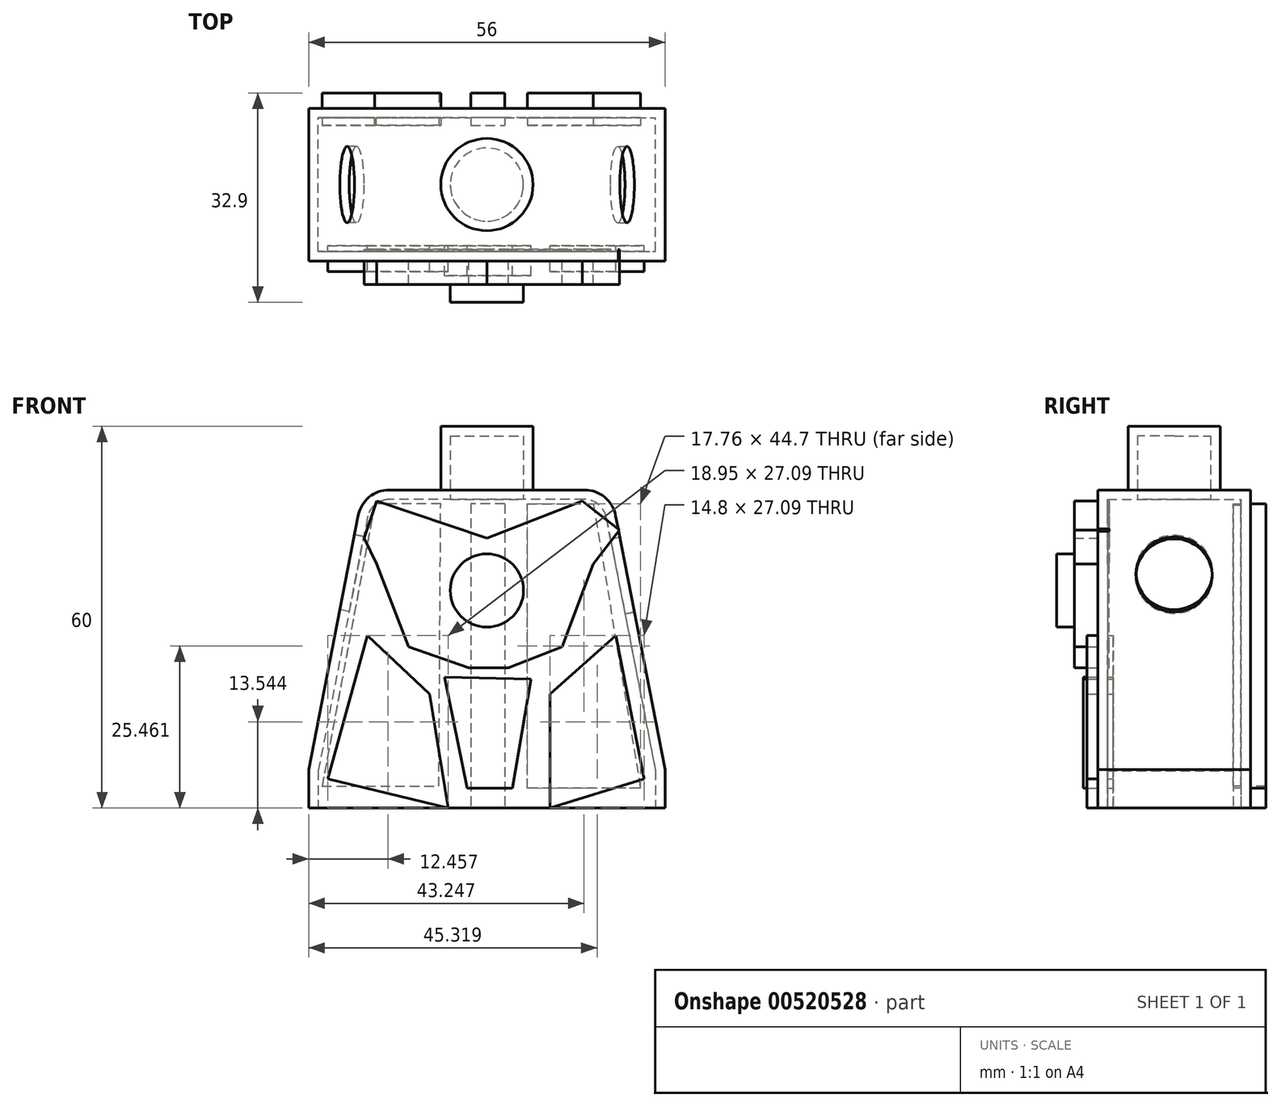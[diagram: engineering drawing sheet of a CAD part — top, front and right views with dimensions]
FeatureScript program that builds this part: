
annotation { "Feature Type Name" : "Feature", "Feature Type Description" : "" }
export const myFeature = defineFeature(function(context is Context, id is Id, definition is map)
    precondition{}
    {
        {
            var Q0;
            Q0=qCreatedBy(makeId("Front.planeOp"),FACE);
            var sketch = newSketch(context, id + "F0", { "sketchPlane" : qUnion([Q0])});
            skLineSegment(sketch, "E0", {"start": v(0, 0) * mm, "end": v(0, 50) * mm});
            skLineSegment(sketch, "E1", {"start": v(0, 50) * mm, "end": v(-6.67, 50) * mm});
            skLineSegment(sketch, "E2", {"start": v(-6.67, 50) * mm, "end": v(-6.67, 50) * mm});
            skLineSegment(sketch, "E3", {"start": v(-6.67, 50) * mm, "end": v(-15.33, 50) * mm});
            skLineSegment(sketch, "E4", {"start": v(-20.23, 45.95) * mm, "end": v(-28, 6) * mm});
            skLineSegment(sketch, "E5", {"start": v(-28, 6) * mm, "end": v(-28, 0) * mm});
            skLineSegment(sketch, "E6", {"start": v(-28, 0) * mm, "end": v(0, 0) * mm});
            skPoint(sketch, "E7.visualSharp", {"position": v(-19.45, 50) * mm});
            skArc(sketch, "E7.filletArc", {"start": v(-15.33, 50) * mm, "mid": v(-18.5, 48.86) * mm, "end": v(-20.23, 45.95) * mm});
            skLineSegment(sketch, "E8", {"start": v(-28, 6) * mm, "end": v(-28, 38.6) * mm, "construction": true});
            skSolve(sketch);
        }
        {
            var Q0;
            Q0=makeQuery(id+"F0.imprint","IMPRINT",FACE,{"disambiguationData":[TD([[makeQuery(id+"F0.imprint","IMPRINT",EDGE,{"derivedFrom":sQuery(id+"F0.wireOp",EDGE,"E0")}),1.0]])]});
            extrude(context, id + "F1", {"entities" : qUnion([Q0]), "endBound" : BoundingType.SYMMETRIC, "depth" : 24 * mm});
        }
        {
            var Q0;
            Q0=makeQuery(id+"F1.opExtrude","SWEPT_BODY",BODY,{"disambiguationData":[OSD([sQuery(id+"F0.wireOp",EDGE,"E0"),sQuery(id+"F0.wireOp",EDGE,"E1"),sQuery(id+"F0.wireOp",EDGE,"E2"),sQuery(id+"F0.wireOp",EDGE,"E3"),sQuery(id+"F0.wireOp",EDGE,"E4"),sQuery(id+"F0.wireOp",EDGE,"E5"),sQuery(id+"F0.wireOp",EDGE,"E6"),sQuery(id+"F0.wireOp",EDGE,"E7.filletArc")])]});
            var Q1;
            Q1=qCreatedBy(makeId("Right.planeOp"),FACE);
            mirror(context, id + "F2", {"operationType" : NewBodyOperationType.ADD, "entities" : qUnion([Q0]), "mirrorPlane" : qUnion([Q1])});
        }
        {
            var Q0;
            {var subQ0=makeQuery(id+"F1.opExtrude","SWEPT_FACE",FACE,{"disambiguationData":[OSD([sQuery(id+"F0.wireOp",EDGE,"E1"),sQuery(id+"F0.wireOp",EDGE,"E3")])]});Q0=makeQuery(id+"F2.boolean.opBoolean","MERGE",FACE,{"derivedFrom":[subQ0,makeQuery(id+"F2.opPattern","COPY",FACE,{"derivedFrom":subQ0,"instanceName":"1"})]});}
            var sketch = newSketch(context, id + "F3", { "sketchPlane" : qUnion([Q0])});
            skCircle(sketch, "E9", {"center": v(0, 0) * mm, "radius": 7.25 * mm});
            skSolve(sketch);
        }
        {
            var Q0;
            Q0=makeQuery(id+"F3.imprint","IMPRINT",FACE,{"disambiguationData":[TD([[makeQuery(id+"F3.imprint","IMPRINT",EDGE,{"derivedFrom":sQuery(id+"F3.wireOp",EDGE,"E9")}),1.0]])]});
            var Q1;
            Q1=sQuery(id+"F3.wireOp",EDGE,"E9");
            extrude(context, id + "F4", {"entities" : qUnion([Q0]), "operationType" : NewBodyOperationType.ADD, "surfaceEntities" : qUnion([Q1]), "depth" : 10 * mm});
        }
        {
            var Q0;
            {var subQ0=makeQuery(id+"F1.opExtrude","SWEPT_FACE",FACE,{"disambiguationData":[OSD([sQuery(id+"F0.wireOp",EDGE,"E6")])]});Q0=makeQuery(id+"F2.boolean.opBoolean","MERGE",FACE,{"derivedFrom":[subQ0,makeQuery(id+"F2.opPattern","COPY",FACE,{"derivedFrom":subQ0,"instanceName":"1"})]});}
            shell(context, id + "F5", {"entities" : qUnion([Q0]), "thickness" : 1.5 * mm});
        }
        {
            var Q0;
            Q0=makeQuery(id+"F2.opPattern","COPY",FACE,{"derivedFrom":makeQuery(id+"F1.opExtrude","SWEPT_FACE",FACE,{"disambiguationData":[OSD([sQuery(id+"F0.wireOp",EDGE,"E4")])]}),"instanceName":"1"});
            var sketch = newSketch(context, id + "F6", { "sketchPlane" : qUnion([Q0])});
            skCircle(sketch, "E10", {"center": v(0, 31.83) * mm, "radius": 6 * mm});
            skSolve(sketch);
        }
        {
            var Q0;
            Q0=makeQuery(id+"F1.opExtrude","SWEPT_FACE",FACE,{"disambiguationData":[OSD([sQuery(id+"F0.wireOp",EDGE,"E4")])]});
            var sketch = newSketch(context, id + "F7", { "sketchPlane" : qUnion([Q0])});
            skCircle(sketch, "E11", {"center": v(0, 32.18) * mm, "radius": 6 * mm});
            skSolve(sketch);
        }
        {
            var Q0;
            Q0=qSketchRegion(id+"F7",true);
            extrude(context, id + "F8", {"entities" : qUnion([Q0]), "operationType" : NewBodyOperationType.REMOVE, "oppositeDirection" : true, "depth" : 25 * mm});
        }
        {
            var Q0;
            Q0=qSketchRegion(id+"F6",true);
            extrude(context, id + "F9", {"entities" : qUnion([Q0]), "operationType" : NewBodyOperationType.REMOVE, "oppositeDirection" : true, "depth" : 25 * mm});
        }
        {
            var Q0;
            Q0=qCreatedBy(makeId("Front.planeOp"),FACE);
            var sketch = newSketch(context, id + "F10", { "sketchPlane" : qUnion([Q0])});
            skLineSegment(sketch, "E12", {"start": v(-17.32, 38.34) * mm, "end": v(-12.29, 25.31) * mm});
            skLineSegment(sketch, "E13", {"start": v(-12.29, 25.31) * mm, "end": v(-2.81, 22.06) * mm});
            skLineSegment(sketch, "E14", {"start": v(-2.81, 22.06) * mm, "end": v(0, 22.06) * mm});
            skLineSegment(sketch, "E15", {"start": v(0, 22.06) * mm, "end": v(3.4, 22.06) * mm});
            skLineSegment(sketch, "E16", {"start": v(3.4, 22.06) * mm, "end": v(11.83, 25.31) * mm});
            skLineSegment(sketch, "E17", {"start": v(11.83, 25.31) * mm, "end": v(16.73, 38.34) * mm});
            skLineSegment(sketch, "E18", {"start": v(16.73, 38.34) * mm, "end": v(20.87, 43.67) * mm});
            skLineSegment(sketch, "E19", {"start": v(20.87, 43.67) * mm, "end": v(15, 48.23) * mm});
            skLineSegment(sketch, "E20", {"start": v(15, 48.23) * mm, "end": v(0, 42.43) * mm});
            skLineSegment(sketch, "E21", {"start": v(0, 42.43) * mm, "end": v(-17.32, 48.23) * mm});
            skLineSegment(sketch, "E22", {"start": v(-17.32, 48.23) * mm, "end": v(-19.26, 42.43) * mm});
            skLineSegment(sketch, "E23", {"start": v(-19.26, 42.43) * mm, "end": v(-17.32, 38.34) * mm});
            skSolve(sketch);
        }
        {
            var Q0;
            Q0 = qSketchRegion(id + "F10", true);
            extrude(context, id + "F11", {"entities" : qUnion([Q0]), "operationType" : NewBodyOperationType.ADD, "depth" : 15.7 * mm, "offsetDistance" : 25 * mm, "hasSecondDirection" : true, "secondDirectionOppositeDirection" : false, "secondDirectionDepth" : 10.2 * mm});
        }
        {
            var Q0;
            Q0=qCreatedBy(makeId("Front.planeOp"),FACE);
            var sketch = newSketch(context, id + "F12", { "sketchPlane" : qUnion([Q0])});
            skLineSegment(sketch, "E24", {"start": v(-6.66, 20.58) * mm, "end": v(-3.1, 3.1) * mm});
            skLineSegment(sketch, "E25", {"start": v(-3.1, 3.1) * mm, "end": v(4, 3.1) * mm});
            skLineSegment(sketch, "E26", {"start": v(4, 3.1) * mm, "end": v(6.96, 20.28) * mm});
            skLineSegment(sketch, "E27", {"start": v(6.96, 20.28) * mm, "end": v(-6.66, 20.58) * mm});
            skSolve(sketch);
        }
        {
            var Q0;
            Q0 = qSketchRegion(id + "F12", true);
            extrude(context, id + "F13", {"entities" : qUnion([Q0]), "operationType" : NewBodyOperationType.ADD, "depth" : 14.3 * mm, "offsetDistance" : 25 * mm, "hasSecondDirection" : true, "secondDirectionOppositeDirection" : false, "secondDirectionDepth" : 9.6 * mm});
        }
        {
            var Q0;
            Q0=qCreatedBy(makeId("Front.planeOp"),FACE);
            var sketch = newSketch(context, id + "F14", { "sketchPlane" : qUnion([Q0])});
            skLineSegment(sketch, "E28", {"start": v(-18.8, 27.09) * mm, "end": v(-9.03, 17.91) * mm});
            skLineSegment(sketch, "E29", {"start": v(-9.03, 17.91) * mm, "end": v(-6.07, 0) * mm});
            skLineSegment(sketch, "E30", {"start": v(-6.07, 0) * mm, "end": v(-25.02, 4.59) * mm});
            skLineSegment(sketch, "E31", {"start": v(-25.02, 4.59) * mm, "end": v(-18.8, 27.09) * mm});
            skLineSegment(sketch, "E32", {"start": v(20.28, 27.09) * mm, "end": v(24.72, 4.59) * mm});
            skLineSegment(sketch, "E33", {"start": v(24.72, 4.59) * mm, "end": v(9.92, 0) * mm});
            skLineSegment(sketch, "E34", {"start": v(9.92, 0) * mm, "end": v(9.92, 17.91) * mm});
            skLineSegment(sketch, "E35", {"start": v(9.92, 17.91) * mm, "end": v(20.28, 27.09) * mm});
            skSolve(sketch);
        }
        {
            var Q0;
            Q0 = qSketchRegion(id + "F14", true);
            extrude(context, id + "F15", {"entities" : qUnion([Q0]), "operationType" : NewBodyOperationType.ADD, "depth" : 13.7 * mm, "offsetDistance" : 25 * mm, "hasSecondDirection" : true, "secondDirectionOppositeDirection" : false, "secondDirectionDepth" : 9.6 * mm});
        }
        {
            var Q0;
            Q0=qCreatedBy(makeId("Front.planeOp"),FACE);
            var sketch = newSketch(context, id + "F16", { "sketchPlane" : qUnion([Q0])});
            skLineSegment(sketch, "E36", {"start": v(2.81, 47.81) * mm, "end": v(2.81, 0) * mm});
            skLineSegment(sketch, "E37", {"start": v(2.81, 47.81) * mm, "end": v(-2.52, 47.81) * mm});
            skLineSegment(sketch, "E38", {"start": v(-2.52, 47.81) * mm, "end": v(-2.52, 0) * mm});
            skLineSegment(sketch, "E39", {"start": v(-2.52, 0) * mm, "end": v(2.81, 0) * mm});
            skLineSegment(sketch, "E40", {"start": v(16.73, 47.81) * mm, "end": v(24.13, 3.1) * mm});
            skLineSegment(sketch, "E41", {"start": v(24.13, 3.1) * mm, "end": v(6.37, 3.1) * mm});
            skLineSegment(sketch, "E42", {"start": v(6.37, 3.1) * mm, "end": v(6.37, 47.81) * mm});
            skLineSegment(sketch, "E43", {"start": v(6.37, 47.81) * mm, "end": v(16.73, 47.81) * mm});
            skLineSegment(sketch, "E44", {"start": v(-7.25, 47.81) * mm, "end": v(-17.62, 47.81) * mm});
            skLineSegment(sketch, "E45", {"start": v(-17.62, 47.81) * mm, "end": v(-25.9, 3.4) * mm});
            skLineSegment(sketch, "E46", {"start": v(-25.9, 3.4) * mm, "end": v(-7.55, 3.4) * mm});
            skLineSegment(sketch, "E47", {"start": v(-7.55, 3.4) * mm, "end": v(-7.25, 47.81) * mm});
            skSolve(sketch);
        }
        {
            var Q0;
            Q0 = qSketchRegion(id + "F16", true);
            extrude(context, id + "F17", {"entities" : qUnion([Q0]), "operationType" : NewBodyOperationType.ADD, "oppositeDirection" : true, "depth" : 14.4 * mm, "offsetDistance" : 25 * mm, "hasSecondDirection" : true, "secondDirectionOppositeDirection" : true, "secondDirectionDepth" : 9.3 * mm});
        }
        {
            var Q0;
            Q0=qCreatedBy(makeId("Front.planeOp"),FACE);
            var sketch = newSketch(context, id + "F18", { "sketchPlane" : qUnion([Q0])});
            skCircle(sketch, "E48", {"center": v(0, 34.2) * mm, "radius": 5.76 * mm});
            skSolve(sketch);
        }
        {
            var Q0;
            Q0 = qSketchRegion(id + "F18", true);
            extrude(context, id + "F19", {"entities" : qUnion([Q0]), "operationType" : NewBodyOperationType.ADD, "depth" : 18.5 * mm, "offsetDistance" : 25 * mm, "hasSecondDirection" : true, "secondDirectionOppositeDirection" : false, "secondDirectionDepth" : 13.2 * mm});
        }
    });
